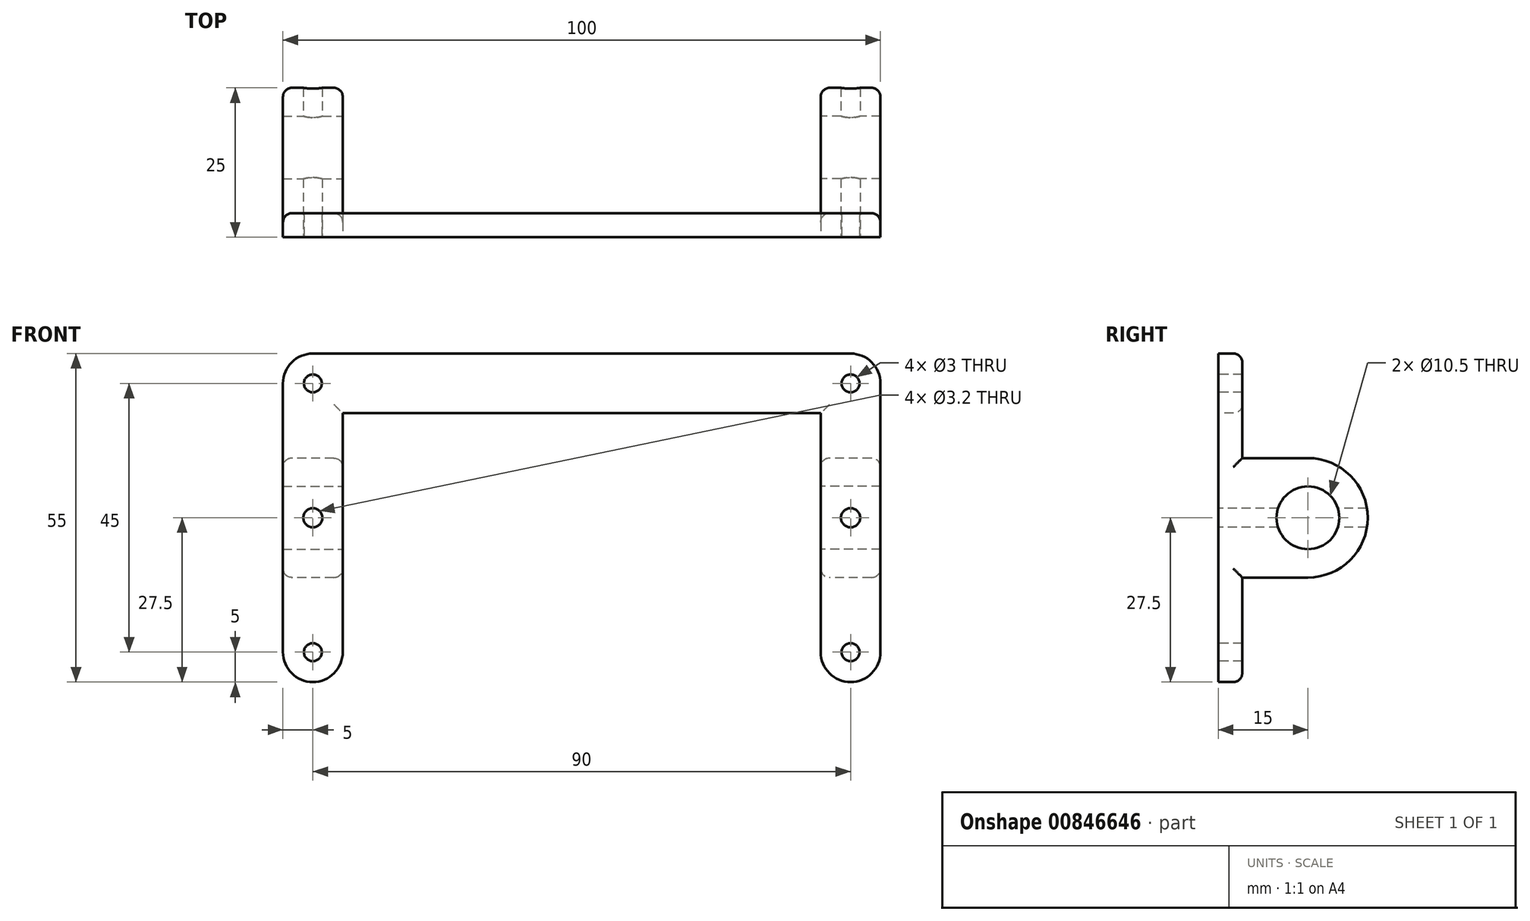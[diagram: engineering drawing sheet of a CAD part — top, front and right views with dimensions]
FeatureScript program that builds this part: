
annotation { "Feature Type Name" : "Feature", "Feature Type Description" : "" }
export const myFeature = defineFeature(function(context is Context, id is Id, definition is map)
    precondition{}
    {
        {
            var Q0;
            Q0=qCreatedBy(makeId("Front.planeOp"),FACE);
            var sketch = newSketch(context, id + "F0", { "sketchPlane" : qUnion([Q0])});
            skLineSegment(sketch, "E0.bottom", {"start": v(0, 0) * mm, "end": v(10, 0) * mm});
            skLineSegment(sketch, "E0.top", {"start": v(0, 55) * mm, "end": v(10, 55) * mm});
            skLineSegment(sketch, "E0.left", {"start": v(0, 0) * mm, "end": v(0, 55) * mm});
            skLineSegment(sketch, "E0.right", {"start": v(10, 0) * mm, "end": v(10, 55) * mm});
            skPoint(sketch, "E1", {"position": v(5, 55) * mm});
            skLineSegment(sketch, "E2", {"start": v(5, 55) * mm, "end": v(5, 0) * mm});
            skLineSegment(sketch, "E3", {"start": v(0, 5) * mm, "end": v(10, 5) * mm});
            skPoint(sketch, "E4", {"position": v(5, 50) * mm});
            skPoint(sketch, "E5", {"position": v(5, 5) * mm});
            skPoint(sketch, "E6", {"position": v(-80, 0) * mm});
            skLineSegment(sketch, "E7.bottom", {"start": v(-90, 55) * mm, "end": v(-80, 55) * mm});
            skLineSegment(sketch, "E7.top", {"start": v(-90, 0) * mm, "end": v(-80, 0) * mm});
            skLineSegment(sketch, "E7.left", {"start": v(-90, 55) * mm, "end": v(-90, 0) * mm});
            skLineSegment(sketch, "E7.right", {"start": v(-80, 55) * mm, "end": v(-80, 0) * mm});
            skLineSegment(sketch, "E8", {"start": v(-85, 55) * mm, "end": v(-85, 0) * mm});
            skLineSegment(sketch, "E9", {"start": v(-90, 45) * mm, "end": v(10, 45) * mm});
            skPoint(sketch, "E10", {"position": v(-85, 50) * mm});
            skPoint(sketch, "E11", {"position": v(-85, 5) * mm});
            skLineSegment(sketch, "E12", {"start": v(0, 55) * mm, "end": v(-80, 55) * mm});
            skLineSegment(sketch, "E13", {"start": v(10, 10) * mm, "end": v(0, 10) * mm});
            skLineSegment(sketch, "E14", {"start": v(-80, 10) * mm, "end": v(-90, 10) * mm});
            skLineSegment(sketch, "E15.bottom", {"start": v(-99.33, 55) * mm, "end": v(-109.33, 55) * mm});
            skLineSegment(sketch, "E15.top", {"start": v(-99.33, 0) * mm, "end": v(-109.33, 0) * mm});
            skLineSegment(sketch, "E15.left", {"start": v(-99.33, 55) * mm, "end": v(-99.33, 0) * mm});
            skLineSegment(sketch, "E15.right", {"start": v(-109.33, 55) * mm, "end": v(-109.33, 0) * mm});
            skLineSegment(sketch, "E16.bottom", {"start": v(-122.4, 55) * mm, "end": v(-132.4, 55) * mm});
            skLineSegment(sketch, "E16.top", {"start": v(-122.4, 0) * mm, "end": v(-132.4, 0) * mm});
            skLineSegment(sketch, "E16.left", {"start": v(-122.4, 55) * mm, "end": v(-122.4, 0) * mm});
            skLineSegment(sketch, "E16.right", {"start": v(-132.4, 55) * mm, "end": v(-132.4, 0) * mm});
            skPoint(sketch, "E17", {"position": v(-104.33, 50) * mm});
            skPoint(sketch, "E18", {"position": v(-127.4, 50) * mm});
            skPoint(sketch, "E19", {"position": v(-104.33, 5) * mm});
            skPoint(sketch, "E20", {"position": v(-127.4, 5) * mm});
            skSolve(sketch);
        }
        {
            var Q0;
            {var subQ0=sQuery(id+"F0.wireOp",EDGE,"Z6pQRhZK-WyxS-twrl-oDdU-gN6A7DWA0EFC");Q0=makeQuery(id+"F0.imprint","IMPRINT",FACE,{"disambiguationData":[TD([[makeQuery(id+"F0.imprint","IMPRINT",EDGE,{"derivedFrom":subQ0}),-1.0]])]});}
            var Q1;
            {var subQ1=sQuery(id+"F0.wireOp",EDGE,"E7.bottom");var subQ3=sQuery(id+"F0.wireOp",EDGE,"E8");var subQ4=makeQuery(id+"F0.imprint","INTERSECT",VERTEX,{"derivedFrom":[subQ1,subQ3]});Q1=makeQuery(id+"F0.imprint","IMPRINT",FACE,{"disambiguationData":[TD([[makeQuery(id+"F0.imprint","IMPRINT",EDGE,{"disambiguationData":[TD([[subQ4,-1.0]])],"derivedFrom":subQ3}),1.0]])]});}
            var Q2;
            {var subQ0=sQuery(id+"F0.wireOp",EDGE,"E7.left");var subQ1=sQuery(id+"F0.wireOp",EDGE,"E7.bottom");var subQ2=makeQuery(id+"F0.imprint","INTERSECT",VERTEX,{"derivedFrom":[subQ1,subQ0]});Q2=makeQuery(id+"F0.imprint","IMPRINT",FACE,{"disambiguationData":[TD([[makeQuery(id+"F0.imprint","IMPRINT",EDGE,{"disambiguationData":[TD([[subQ2,-1.0]])],"derivedFrom":subQ1}),-1.0]])]});}
            var Q3;
            {var subQ0=sQuery(id+"F0.wireOp",EDGE,"E7.left");var subQ1=sQuery(id+"F0.wireOp",EDGE,"E7.top");var subQ2=makeQuery(id+"F0.imprint","INTERSECT",VERTEX,{"derivedFrom":[subQ1,subQ0]});Q3=makeQuery(id+"F0.imprint","IMPRINT",FACE,{"disambiguationData":[TD([[makeQuery(id+"F0.imprint","IMPRINT",EDGE,{"disambiguationData":[TD([[subQ2,-1.0]])],"derivedFrom":subQ1}),1.0]])]});}
            var Q4;
            {var subQ0=sQuery(id+"F0.wireOp",EDGE,"E7.right");var subQ1=sQuery(id+"F0.wireOp",EDGE,"E7.top");var subQ2=makeQuery(id+"F0.imprint","INTERSECT",VERTEX,{"derivedFrom":[subQ1,subQ0]});Q4=makeQuery(id+"F0.imprint","IMPRINT",FACE,{"disambiguationData":[TD([[makeQuery(id+"F0.imprint","IMPRINT",EDGE,{"disambiguationData":[TD([[subQ2,1.0]])],"derivedFrom":subQ1}),1.0]])]});}
            var Q5;
            {var subQ1=sQuery(id+"F0.wireOp",EDGE,"E0.top");var subQ3=sQuery(id+"F0.wireOp",EDGE,"E2");var subQ4=makeQuery(id+"F0.imprint","INTERSECT",VERTEX,{"derivedFrom":[subQ1,subQ3]});Q5=makeQuery(id+"F0.imprint","IMPRINT",FACE,{"disambiguationData":[TD([[makeQuery(id+"F0.imprint","IMPRINT",EDGE,{"disambiguationData":[TD([[subQ4,-1.0]])],"derivedFrom":subQ3}),-1.0]])]});}
            var Q6;
            {var subQ0=sQuery(id+"F0.wireOp",EDGE,"E0.right");var subQ1=sQuery(id+"F0.wireOp",EDGE,"E0.top");var subQ2=makeQuery(id+"F0.imprint","INTERSECT",VERTEX,{"derivedFrom":[subQ1,subQ0]});Q6=makeQuery(id+"F0.imprint","IMPRINT",FACE,{"disambiguationData":[TD([[makeQuery(id+"F0.imprint","IMPRINT",EDGE,{"disambiguationData":[TD([[subQ2,1.0]])],"derivedFrom":subQ1}),-1.0]])]});}
            var Q7;
            {var subQ0=sQuery(id+"F0.wireOp",EDGE,"E3");var subQ1=sQuery(id+"F0.wireOp",EDGE,"E0.left");var subQ2=makeQuery(id+"F0.imprint","INTERSECT",VERTEX,{"derivedFrom":[subQ1,subQ0]});Q7=makeQuery(id+"F0.imprint","IMPRINT",FACE,{"disambiguationData":[TD([[makeQuery(id+"F0.imprint","IMPRINT",EDGE,{"disambiguationData":[TD([[subQ2,-1.0]])],"derivedFrom":subQ1}),-1.0]])]});}
            var Q8;
            {var subQ0=sQuery(id+"F0.wireOp",EDGE,"E3");var subQ1=sQuery(id+"F0.wireOp",EDGE,"E0.right");var subQ2=makeQuery(id+"F0.imprint","INTERSECT",VERTEX,{"derivedFrom":[subQ1,subQ0]});Q8=makeQuery(id+"F0.imprint","IMPRINT",FACE,{"disambiguationData":[TD([[makeQuery(id+"F0.imprint","IMPRINT",EDGE,{"disambiguationData":[TD([[subQ2,-1.0]])],"derivedFrom":subQ1}),1.0]])]});}
            var Q9;
            {var subQ0=sQuery(id+"F0.wireOp",EDGE,"E0.right");var subQ1=sQuery(id+"F0.wireOp",EDGE,"E0.bottom");var subQ2=makeQuery(id+"F0.imprint","INTERSECT",VERTEX,{"derivedFrom":[subQ1,subQ0]});Q9=makeQuery(id+"F0.imprint","IMPRINT",FACE,{"disambiguationData":[TD([[makeQuery(id+"F0.imprint","IMPRINT",EDGE,{"disambiguationData":[TD([[subQ2,1.0]])],"derivedFrom":subQ1}),1.0]])]});}
            var Q10;
            {var subQ0=sQuery(id+"F0.wireOp",EDGE,"E0.left");var subQ1=sQuery(id+"F0.wireOp",EDGE,"E0.bottom");var subQ2=makeQuery(id+"F0.imprint","INTERSECT",VERTEX,{"derivedFrom":[subQ1,subQ0]});Q10=makeQuery(id+"F0.imprint","IMPRINT",FACE,{"disambiguationData":[TD([[makeQuery(id+"F0.imprint","IMPRINT",EDGE,{"disambiguationData":[TD([[subQ2,-1.0]])],"derivedFrom":subQ1}),1.0]])]});}
            var Q11;
            {var subQ0=sQuery(id+"F0.wireOp",EDGE,"58kG1eCo-gTD1-qcwa-fSQV-I8Bj7SWHsk2V");Q11=makeQuery(id+"F0.imprint","IMPRINT",FACE,{"disambiguationData":[TD([[makeQuery(id+"F0.imprint","IMPRINT",EDGE,{"derivedFrom":subQ0}),1.0]])]});}
            var Q12;
            {var subQ0=sQuery(id+"F0.wireOp",EDGE,"E12");Q12=makeQuery(id+"F0.imprint","IMPRINT",FACE,{"disambiguationData":[TD([[makeQuery(id+"F0.imprint","IMPRINT",EDGE,{"derivedFrom":subQ0}),1.0]])]});}
            var Q13;
            {var subQ0=sQuery(id+"F0.wireOp",EDGE,"E13");var subQ1=sQuery(id+"F0.wireOp",EDGE,"E0.left");var subQ2=makeQuery(id+"F0.imprint","INTERSECT",VERTEX,{"derivedFrom":[subQ1,subQ0]});Q13=makeQuery(id+"F0.imprint","IMPRINT",FACE,{"disambiguationData":[TD([[makeQuery(id+"F0.imprint","IMPRINT",EDGE,{"disambiguationData":[TD([[subQ2,-1.0]])],"derivedFrom":subQ1}),-1.0]])]});}
            var Q14;
            {var subQ0=sQuery(id+"F0.wireOp",EDGE,"E9");var subQ1=sQuery(id+"F0.wireOp",EDGE,"E0.right");var subQ2=makeQuery(id+"F0.imprint","INTERSECT",VERTEX,{"derivedFrom":[subQ1,subQ0]});Q14=makeQuery(id+"F0.imprint","IMPRINT",FACE,{"disambiguationData":[TD([[makeQuery(id+"F0.imprint","IMPRINT",EDGE,{"disambiguationData":[TD([[subQ2,1.0]])],"derivedFrom":subQ1}),1.0]])]});}
            var Q15;
            {var subQ0=sQuery(id+"F0.wireOp",EDGE,"E14");var subQ1=sQuery(id+"F0.wireOp",EDGE,"E7.right");var subQ2=makeQuery(id+"F0.imprint","INTERSECT",VERTEX,{"derivedFrom":[subQ1,subQ0]});Q15=makeQuery(id+"F0.imprint","IMPRINT",FACE,{"disambiguationData":[TD([[makeQuery(id+"F0.imprint","IMPRINT",EDGE,{"disambiguationData":[TD([[subQ2,1.0]])],"derivedFrom":subQ1}),-1.0]])]});}
            var Q16;
            {var subQ0=sQuery(id+"F0.wireOp",EDGE,"E9");var subQ1=sQuery(id+"F0.wireOp",EDGE,"E7.left");var subQ2=makeQuery(id+"F0.imprint","INTERSECT",VERTEX,{"derivedFrom":[subQ1,subQ0]});Q16=makeQuery(id+"F0.imprint","IMPRINT",FACE,{"disambiguationData":[TD([[makeQuery(id+"F0.imprint","IMPRINT",EDGE,{"disambiguationData":[TD([[subQ2,-1.0]])],"derivedFrom":subQ1}),1.0]])]});}
            extrude(context, id + "F1", {"entities" : qUnion([Q0, Q1, Q2, Q3, Q4, Q5, Q6, Q7, Q8, Q9, Q10, Q11, Q12, Q13, Q14, Q15, Q16]), "oppositeDirection" : true, "depth" : 4 * mm, "offsetDistance" : 25 * mm});
        }
        {
            var Q0;
            Q0=qCreatedBy(makeId("Front.planeOp"),FACE);
            var sketch = newSketch(context, id + "F2", { "sketchPlane" : qUnion([Q0])});
            skPoint(sketch, "E21", {"position": v(5, 50) * mm});
            skPoint(sketch, "E22", {"position": v(5, 5) * mm});
            skPoint(sketch, "E23", {"position": v(-85, 50) * mm});
            skPoint(sketch, "E24", {"position": v(-85, 5) * mm});
            skSolve(sketch);
        }
        {
            var Q0;
            Q0=sQuery(id+"F2.wireOp",VERTEX,"E21");
            var Q1;
            Q1=sQuery(id+"F2.wireOp",VERTEX,"E23");
            var Q2;
            Q2=sQuery(id+"F2.wireOp",VERTEX,"E22");
            var Q3;
            Q3=sQuery(id+"F2.wireOp",VERTEX,"E24");
            var Q4;
            Q4=makeQuery(id+"F1.opExtrude","SWEPT_BODY",BODY,{"disambiguationData":[OSD([sQuery(id+"F0.wireOp",EDGE,"E0.bottom"),sQuery(id+"F0.wireOp",EDGE,"E0.top"),sQuery(id+"F0.wireOp",EDGE,"E0.left"),sQuery(id+"F0.wireOp",EDGE,"E0.right"),sQuery(id+"F0.wireOp",EDGE,"E7.bottom"),sQuery(id+"F0.wireOp",EDGE,"E7.top"),sQuery(id+"F0.wireOp",EDGE,"E7.left"),sQuery(id+"F0.wireOp",EDGE,"E7.right"),sQuery(id+"F0.wireOp",EDGE,"E9"),sQuery(id+"F0.wireOp",EDGE,"E12")])]});
            hole(context, id + "F3", {"style" : HoleStyle.SIMPLE, "endStyle" : HoleEndStyle.THROUGH, "holeDiameter" : 3 * mm, "majorDiameter" : 5 * mm, "isTappedThrough" : true, "tappedDepth" : 12 * mm, "tapClearance" : 3, "locations" : qUnion([Q0, Q1, Q2, Q3]), "scope" : qUnion([Q4])});
        }
        {
            var Q0;
            Q0=qCreatedBy(makeId("Front.planeOp"),FACE);
            var sketch = newSketch(context, id + "F4", { "sketchPlane" : qUnion([Q0])});
            skPoint(sketch, "E25", {"position": v(10, 27.5) * mm});
            skLineSegment(sketch, "E26", {"start": v(10, 27.5) * mm, "end": v(-90, 27.5) * mm});
            skLineSegment(sketch, "E27.bottom", {"start": v(10, 37.5) * mm, "end": v(0, 37.5) * mm});
            skLineSegment(sketch, "E27.top", {"start": v(10, 17.5) * mm, "end": v(0, 17.5) * mm});
            skLineSegment(sketch, "E27.left", {"start": v(10, 37.5) * mm, "end": v(10, 17.5) * mm});
            skLineSegment(sketch, "E27.right", {"start": v(0, 37.5) * mm, "end": v(0, 17.5) * mm});
            skLineSegment(sketch, "E28", {"start": v(-80, 37.5) * mm, "end": v(-90, 37.5) * mm});
            skLineSegment(sketch, "E29", {"start": v(-80, 17.5) * mm, "end": v(-90, 17.5) * mm});
            skLineSegment(sketch, "E30", {"start": v(-80, 37.5) * mm, "end": v(-80, 17.5) * mm});
            skLineSegment(sketch, "E31", {"start": v(-90, 37.5) * mm, "end": v(-90, 17.5) * mm});
            skSolve(sketch);
        }
        {
            var Q0;
            Q0 = qSketchRegion(id + "F4", true);
            extrude(context, id + "F5", {"entities" : qUnion([Q0]), "operationType" : NewBodyOperationType.ADD, "oppositeDirection" : true, "depth" : 25 * mm, "offsetDistance" : 25 * mm});
        }
        {
            var Q0;
            Q0=qCreatedBy(makeId("Right.planeOp"),FACE);
            var sketch = newSketch(context, id + "F6", { "sketchPlane" : qUnion([Q0])});
            skPoint(sketch, "E32", {"position": v(15, 27.5) * mm});
            skSolve(sketch);
        }
        {
            var Q0;
            Q0=sQuery(id+"F6.wireOp",VERTEX,"E32");
            var Q1;
            Q1=makeQuery(id+"F1.opExtrude","SWEPT_BODY",BODY,{"disambiguationData":[OSD([sQuery(id+"F0.wireOp",EDGE,"E0.bottom"),sQuery(id+"F0.wireOp",EDGE,"E0.top"),sQuery(id+"F0.wireOp",EDGE,"E0.left"),sQuery(id+"F0.wireOp",EDGE,"E0.right"),sQuery(id+"F0.wireOp",EDGE,"E7.bottom"),sQuery(id+"F0.wireOp",EDGE,"E7.top"),sQuery(id+"F0.wireOp",EDGE,"E7.left"),sQuery(id+"F0.wireOp",EDGE,"E7.right"),sQuery(id+"F0.wireOp",EDGE,"E9"),sQuery(id+"F0.wireOp",EDGE,"E12")])]});
            hole(context, id + "F7", {"style" : HoleStyle.SIMPLE, "endStyle" : HoleEndStyle.THROUGH, "oppositeDirection" : true, "holeDiameter" : 10.5 * mm, "majorDiameter" : 5 * mm, "isTappedThrough" : true, "tappedDepth" : 12 * mm, "tapClearance" : 3, "locations" : qUnion([Q0]), "scope" : qUnion([Q1])});
        }
        {
            var Q0;
            Q0=qCreatedBy(makeId("Right.planeOp"),FACE);
            var sketch = newSketch(context, id + "F8", { "sketchPlane" : qUnion([Q0])});
            skPoint(sketch, "E33", {"position": v(15, 27.5) * mm});
            skSolve(sketch);
        }
        {
            var Q0;
            Q0=sQuery(id+"F8.wireOp",VERTEX,"E33");
            var Q1;
            Q1=makeQuery(id+"F1.opExtrude","SWEPT_BODY",BODY,{"disambiguationData":[OSD([sQuery(id+"F0.wireOp",EDGE,"E0.bottom"),sQuery(id+"F0.wireOp",EDGE,"E0.top"),sQuery(id+"F0.wireOp",EDGE,"E0.left"),sQuery(id+"F0.wireOp",EDGE,"E0.right"),sQuery(id+"F0.wireOp",EDGE,"E7.bottom"),sQuery(id+"F0.wireOp",EDGE,"E7.top"),sQuery(id+"F0.wireOp",EDGE,"E7.left"),sQuery(id+"F0.wireOp",EDGE,"E7.right"),sQuery(id+"F0.wireOp",EDGE,"E9"),sQuery(id+"F0.wireOp",EDGE,"E12")])]});
            hole(context, id + "F9", {"style" : HoleStyle.SIMPLE, "endStyle" : HoleEndStyle.THROUGH, "holeDiameter" : 10.5 * mm, "majorDiameter" : 5 * mm, "isTappedThrough" : true, "tappedDepth" : 12 * mm, "tapClearance" : 3, "locations" : qUnion([Q0]), "scope" : qUnion([Q1])});
        }
        {
            var Q0;
            Q0=makeQuery(id+"F5.opExtrude","CAP_EDGE",EDGE,{"disambiguationData":[OSD([sQuery(id+"F4.wireOp",EDGE,"E27.bottom")])],"isStart":false});
            var Q1;
            Q1=makeQuery(id+"F5.opExtrude","CAP_EDGE",EDGE,{"disambiguationData":[OSD([sQuery(id+"F4.wireOp",EDGE,"E27.top")])],"isStart":false});
            var Q2;
            Q2=makeQuery(id+"F5.opExtrude","CAP_EDGE",EDGE,{"disambiguationData":[OSD([sQuery(id+"F4.wireOp",EDGE,"E28")])],"isStart":false});
            var Q3;
            Q3=makeQuery(id+"F5.opExtrude","CAP_EDGE",EDGE,{"disambiguationData":[OSD([sQuery(id+"F4.wireOp",EDGE,"E29")])],"isStart":false});
            fillet(context, id + "F10", {"entities" : qUnion([Q0, Q1, Q2, Q3]), "radius" : 10 * mm, "tangentPropagation" : true, "allowEdgeOverflow" : false});
        }
        {
            var Q0;
            Q0=makeQuery(id+"F1.opExtrude","SWEPT_EDGE",EDGE,{"disambiguationData":[OSD([sQuery(id+"F0.wireOp",EDGE,"E0.bottom"),sQuery(id+"F0.wireOp",EDGE,"E0.right")])]});
            var Q1;
            Q1=makeQuery(id+"F1.opExtrude","SWEPT_EDGE",EDGE,{"disambiguationData":[OSD([sQuery(id+"F0.wireOp",EDGE,"E7.top"),sQuery(id+"F0.wireOp",EDGE,"E7.left")])]});
            var Q2;
            Q2=makeQuery(id+"F1.opExtrude","SWEPT_EDGE",EDGE,{"disambiguationData":[OSD([sQuery(id+"F0.wireOp",EDGE,"E7.top"),sQuery(id+"F0.wireOp",EDGE,"E7.right")])]});
            var Q3;
            Q3=makeQuery(id+"F1.opExtrude","SWEPT_EDGE",EDGE,{"disambiguationData":[OSD([sQuery(id+"F0.wireOp",EDGE,"E7.bottom"),sQuery(id+"F0.wireOp",EDGE,"E7.left")])]});
            var Q4;
            Q4=makeQuery(id+"F1.opExtrude","SWEPT_EDGE",EDGE,{"disambiguationData":[OSD([sQuery(id+"F0.wireOp",EDGE,"E0.top"),sQuery(id+"F0.wireOp",EDGE,"E0.right")])]});
            var Q5;
            Q5=makeQuery(id+"F1.opExtrude","SWEPT_EDGE",EDGE,{"disambiguationData":[OSD([sQuery(id+"F0.wireOp",EDGE,"E0.bottom"),sQuery(id+"F0.wireOp",EDGE,"E0.left")])]});
            fillet(context, id + "F11", {"entities" : qUnion([Q0, Q1, Q2, Q3, Q4, Q5]), "radius" : 5 * mm, "tangentPropagation" : true, "allowEdgeOverflow" : false});
        }
        {
            var Q0;
            Q0=qCreatedBy(makeId("Front.planeOp"),FACE);
            var sketch = newSketch(context, id + "F12", { "sketchPlane" : qUnion([Q0])});
            skPoint(sketch, "E34", {"position": v(5, 27.5) * mm});
            skPoint(sketch, "E35", {"position": v(-85, 27.5) * mm});
            skSolve(sketch);
        }
        {
            var Q0;
            Q0=sQuery(id+"F12.wireOp",VERTEX,"E34");
            var Q1;
            Q1=sQuery(id+"F12.wireOp",VERTEX,"E35");
            var Q2;
            Q2=makeQuery(id+"F1.opExtrude","SWEPT_BODY",BODY,{"disambiguationData":[OSD([sQuery(id+"F0.wireOp",EDGE,"E0.bottom"),sQuery(id+"F0.wireOp",EDGE,"E0.top"),sQuery(id+"F0.wireOp",EDGE,"E0.left"),sQuery(id+"F0.wireOp",EDGE,"E0.right"),sQuery(id+"F0.wireOp",EDGE,"E7.bottom"),sQuery(id+"F0.wireOp",EDGE,"E7.top"),sQuery(id+"F0.wireOp",EDGE,"E7.left"),sQuery(id+"F0.wireOp",EDGE,"E7.right"),sQuery(id+"F0.wireOp",EDGE,"E9"),sQuery(id+"F0.wireOp",EDGE,"E12")])]});
            hole(context, id + "F13", {"style" : HoleStyle.SIMPLE, "endStyle" : HoleEndStyle.BLIND, "holeDiameter" : 3.2 * mm, "majorDiameter" : 5 * mm, "holeDepth" : 25 * mm, "isTappedThrough" : true, "tappedDepth" : 12 * mm, "tapClearance" : 3, "locations" : qUnion([Q0, Q1]), "scope" : qUnion([Q2])});
        }
        {
            var Q0;
            Q0=makeQuery(id+"F1.opExtrude","CAP_EDGE",EDGE,{"disambiguationData":[OSD([sQuery(id+"F0.wireOp",EDGE,"E0.top"),sQuery(id+"F0.wireOp",EDGE,"E7.bottom"),sQuery(id+"F0.wireOp",EDGE,"E12")])],"isStart":false});
            var Q1;
            Q1=makeQuery(id+"F10.opFillet","BLEND_EDGE",EDGE,{"blendedFrom":[makeQuery(id+"F5.opExtrude","CAP_EDGE",EDGE,{"disambiguationData":[OSD([sQuery(id+"F4.wireOp",EDGE,"E27.bottom")])],"isStart":false}),makeQuery(id+"F5.boolean.opBoolean","MERGE",FACE,{"derivedFrom":[makeQuery(id+"F1.opExtrude","SWEPT_FACE",FACE,{"disambiguationData":[OSD([sQuery(id+"F0.wireOp",EDGE,"E0.right")])]}),makeQuery(id+"F5.opExtrude","SWEPT_FACE",FACE,{"disambiguationData":[OSD([sQuery(id+"F4.wireOp",EDGE,"E27.left")])]})]})],"blendedInto":[makeQuery(id+"F5.boolean.opBoolean","MERGE",FACE,{"derivedFrom":[makeQuery(id+"F1.opExtrude","SWEPT_FACE",FACE,{"disambiguationData":[OSD([sQuery(id+"F0.wireOp",EDGE,"E0.right")])]}),makeQuery(id+"F5.opExtrude","SWEPT_FACE",FACE,{"disambiguationData":[OSD([sQuery(id+"F4.wireOp",EDGE,"E27.left")])]})]})]});
            var Q2;
            {var subQ0=sQuery(id+"F0.wireOp",EDGE,"E0.right");var subQ1=sQuery(id+"F0.wireOp",EDGE,"E0.bottom");Q2=makeQuery(id+"F5.boolean.opBoolean","SPLIT",EDGE,{"disambiguationData":[TD([makeQuery(id+"F1.opExtrude","SWEPT_FACE",FACE,{"disambiguationData":[OSD([subQ1])]})])],"derivedFrom":makeQuery(id+"F1.opExtrude","CAP_EDGE",EDGE,{"disambiguationData":[OSD([subQ0])],"isStart":false})});}
            var Q3;
            Q3=makeQuery(id+"F10.opFillet","BLEND_EDGE",EDGE,{"blendedFrom":[makeQuery(id+"F5.opExtrude","CAP_EDGE",EDGE,{"disambiguationData":[OSD([sQuery(id+"F4.wireOp",EDGE,"E27.bottom")])],"isStart":false}),makeQuery(id+"F5.boolean.opBoolean","MERGE",FACE,{"derivedFrom":[makeQuery(id+"F1.opExtrude","SWEPT_FACE",FACE,{"disambiguationData":[OSD([sQuery(id+"F0.wireOp",EDGE,"E0.left")])]}),makeQuery(id+"F5.opExtrude","SWEPT_FACE",FACE,{"disambiguationData":[OSD([sQuery(id+"F4.wireOp",EDGE,"E27.right")])]})]})],"blendedInto":[makeQuery(id+"F5.boolean.opBoolean","MERGE",FACE,{"derivedFrom":[makeQuery(id+"F1.opExtrude","SWEPT_FACE",FACE,{"disambiguationData":[OSD([sQuery(id+"F0.wireOp",EDGE,"E0.left")])]}),makeQuery(id+"F5.opExtrude","SWEPT_FACE",FACE,{"disambiguationData":[OSD([sQuery(id+"F4.wireOp",EDGE,"E27.right")])]})]})]});
            var Q4;
            {var subQ0=sQuery(id+"F0.wireOp",EDGE,"E9");var subQ1=sQuery(id+"F0.wireOp",EDGE,"E0.left");Q4=makeQuery(id+"F5.boolean.opBoolean","SPLIT",EDGE,{"disambiguationData":[TD([makeQuery(id+"F1.opExtrude","SWEPT_FACE",FACE,{"disambiguationData":[OSD([subQ0])]})])],"derivedFrom":makeQuery(id+"F1.opExtrude","CAP_EDGE",EDGE,{"disambiguationData":[OSD([subQ1])],"isStart":false})});}
            var Q5;
            Q5=makeQuery(id+"F1.opExtrude","CAP_EDGE",EDGE,{"disambiguationData":[OSD([sQuery(id+"F0.wireOp",EDGE,"E9")])],"isStart":false});
            var Q6;
            {var subQ0=sQuery(id+"F0.wireOp",EDGE,"E9");var subQ1=sQuery(id+"F0.wireOp",EDGE,"E7.right");Q6=makeQuery(id+"F5.boolean.opBoolean","SPLIT",EDGE,{"disambiguationData":[TD([makeQuery(id+"F1.opExtrude","SWEPT_FACE",FACE,{"disambiguationData":[OSD([subQ0])]})])],"derivedFrom":makeQuery(id+"F1.opExtrude","CAP_EDGE",EDGE,{"disambiguationData":[OSD([subQ1])],"isStart":false})});}
            var Q7;
            Q7=makeQuery(id+"F10.opFillet","BLEND_EDGE",EDGE,{"blendedFrom":[makeQuery(id+"F5.opExtrude","CAP_EDGE",EDGE,{"disambiguationData":[OSD([sQuery(id+"F4.wireOp",EDGE,"E28")])],"isStart":false}),makeQuery(id+"F5.boolean.opBoolean","MERGE",FACE,{"derivedFrom":[makeQuery(id+"F1.opExtrude","SWEPT_FACE",FACE,{"disambiguationData":[OSD([sQuery(id+"F0.wireOp",EDGE,"E7.right")])]}),makeQuery(id+"F5.opExtrude","SWEPT_FACE",FACE,{"disambiguationData":[OSD([sQuery(id+"F4.wireOp",EDGE,"E30")])]})]})],"blendedInto":[makeQuery(id+"F5.boolean.opBoolean","MERGE",FACE,{"derivedFrom":[makeQuery(id+"F1.opExtrude","SWEPT_FACE",FACE,{"disambiguationData":[OSD([sQuery(id+"F0.wireOp",EDGE,"E7.right")])]}),makeQuery(id+"F5.opExtrude","SWEPT_FACE",FACE,{"disambiguationData":[OSD([sQuery(id+"F4.wireOp",EDGE,"E30")])]})]})]});
            var Q8;
            Q8=makeQuery(id+"F10.opFillet","BLEND_EDGE",EDGE,{"blendedFrom":[makeQuery(id+"F5.opExtrude","CAP_EDGE",EDGE,{"disambiguationData":[OSD([sQuery(id+"F4.wireOp",EDGE,"E28")])],"isStart":false}),makeQuery(id+"F5.boolean.opBoolean","MERGE",FACE,{"derivedFrom":[makeQuery(id+"F1.opExtrude","SWEPT_FACE",FACE,{"disambiguationData":[OSD([sQuery(id+"F0.wireOp",EDGE,"E7.left")])]}),makeQuery(id+"F5.opExtrude","SWEPT_FACE",FACE,{"disambiguationData":[OSD([sQuery(id+"F4.wireOp",EDGE,"E31")])]})]})],"blendedInto":[makeQuery(id+"F5.boolean.opBoolean","MERGE",FACE,{"derivedFrom":[makeQuery(id+"F1.opExtrude","SWEPT_FACE",FACE,{"disambiguationData":[OSD([sQuery(id+"F0.wireOp",EDGE,"E7.left")])]}),makeQuery(id+"F5.opExtrude","SWEPT_FACE",FACE,{"disambiguationData":[OSD([sQuery(id+"F4.wireOp",EDGE,"E31")])]})]})]});
            var Q9;
            {var subQ0=sQuery(id+"F0.wireOp",EDGE,"E7.top");var subQ1=sQuery(id+"F0.wireOp",EDGE,"E7.left");Q9=makeQuery(id+"F5.boolean.opBoolean","SPLIT",EDGE,{"disambiguationData":[TD([makeQuery(id+"F1.opExtrude","SWEPT_FACE",FACE,{"disambiguationData":[OSD([subQ0])]})])],"derivedFrom":makeQuery(id+"F1.opExtrude","CAP_EDGE",EDGE,{"disambiguationData":[OSD([subQ1])],"isStart":false})});}
            fillet(context, id + "F14", {"entities" : qUnion([Q0, Q1, Q2, Q3, Q4, Q5, Q6, Q7, Q8, Q9]), "radius" : 1.5 * mm, "tangentPropagation" : true, "allowEdgeOverflow" : false});
        }
    });
